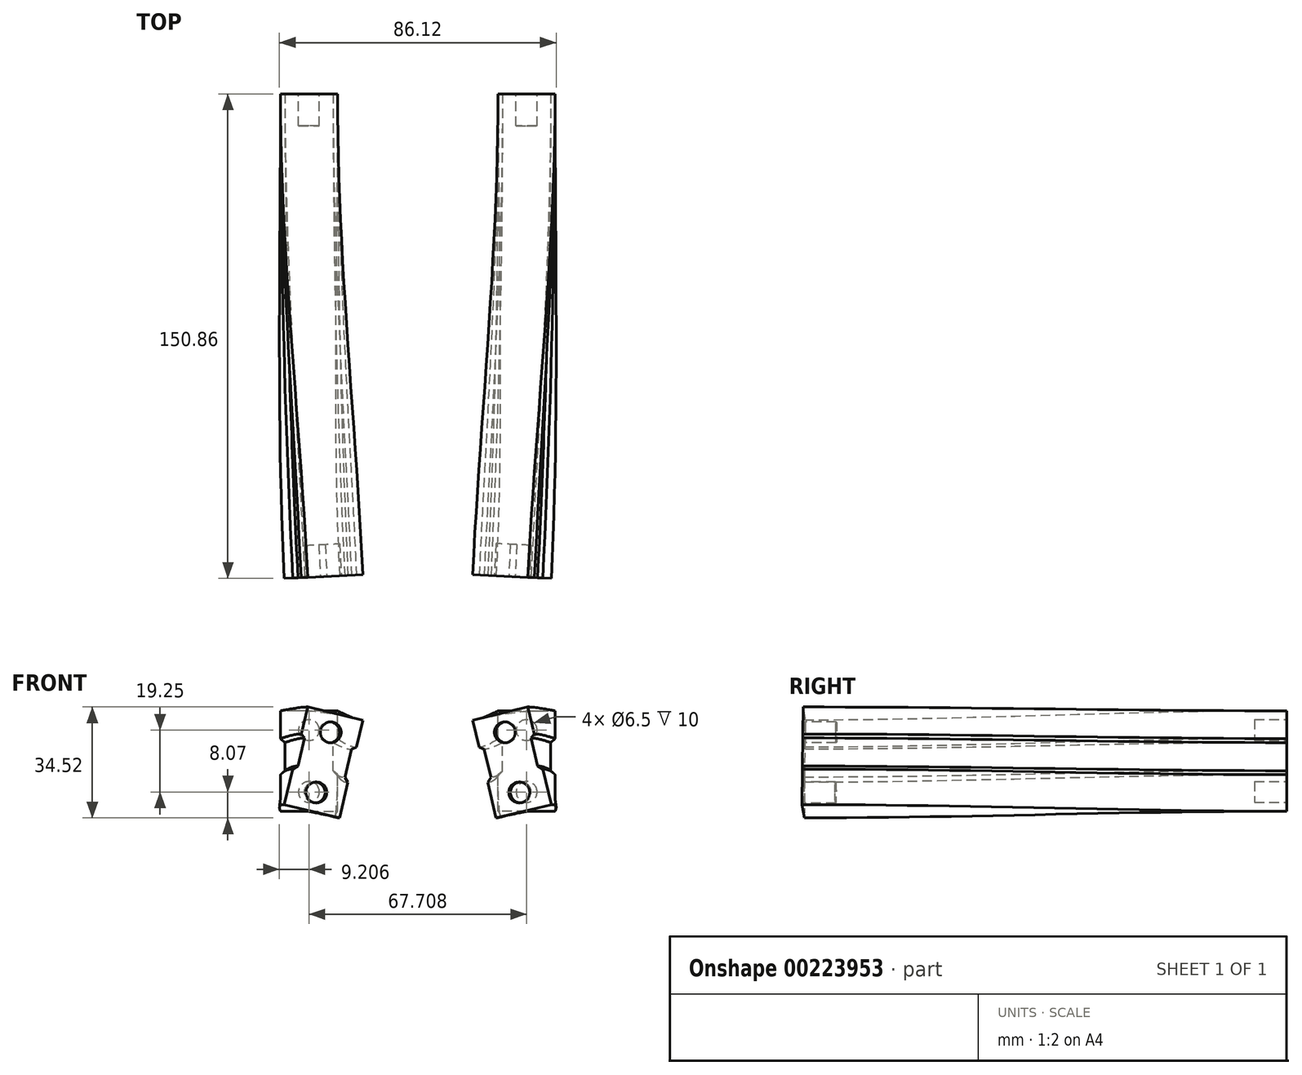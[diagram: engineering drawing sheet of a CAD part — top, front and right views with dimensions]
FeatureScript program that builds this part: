
annotation { "Feature Type Name" : "Feature", "Feature Type Description" : "" }
export const myFeature = defineFeature(function(context is Context, id is Id, definition is map)
    precondition{}
    {
        {
            var Q0;
            Q0=qCreatedBy(makeId("Front.planeOp"),FACE);
            var sketch = newSketch(context, id + "F0", { "sketchPlane" : qUnion([Q0])});
            skLineSegment(sketch, "E0.bottom", {"start": v(0, 0) * mm, "end": v(17.7, 0) * mm, "construction": true});
            skLineSegment(sketch, "E0.top", {"start": v(0, 31.25) * mm, "end": v(17.7, 31.25) * mm, "construction": true});
            skLineSegment(sketch, "E0.left", {"start": v(0, 0) * mm, "end": v(0, 31.25) * mm, "construction": true});
            skLineSegment(sketch, "E0.right", {"start": v(17.7, 0) * mm, "end": v(17.7, 31.25) * mm, "construction": true});
            skLineSegment(sketch, "E1", {"start": v(8.85, 31.25) * mm, "end": v(8.85, 0) * mm, "construction": true});
            skLineSegment(sketch, "E2", {"start": v(8.85, 0) * mm, "end": v(0, 0) * mm});
            skLineSegment(sketch, "E3", {"start": v(0, 11.35) * mm, "end": v(1.35, 12.6) * mm});
            skLineSegment(sketch, "E4", {"start": v(1.35, 12.6) * mm, "end": v(1.35, 21.35) * mm});
            skLineSegment(sketch, "E5", {"start": v(1.35, 21.35) * mm, "end": v(0, 22.6) * mm});
            skLineSegment(sketch, "E6", {"start": v(0, 22.6) * mm, "end": v(0, 31.25) * mm});
            skLineSegment(sketch, "E7", {"start": v(8.85, 31.25) * mm, "end": v(0, 31.25) * mm});
            skLineSegment(sketch, "E8", {"start": v(0, 0) * mm, "end": v(0, 11.35) * mm});
            skLineSegment(sketch, "E9.MirrorCS", {"start": v(16.35, 21.35) * mm, "end": v(17.7, 22.6) * mm});
            skLineSegment(sketch, "E10.MirrorCS", {"start": v(17.7, 11.35) * mm, "end": v(16.35, 12.6) * mm});
            skLineSegment(sketch, "E11.MirrorCS", {"start": v(17.7, 0) * mm, "end": v(17.7, 11.35) * mm});
            skLineSegment(sketch, "E12.MirrorCS", {"start": v(8.85, 31.25) * mm, "end": v(17.7, 31.25) * mm});
            skLineSegment(sketch, "E13.MirrorCS", {"start": v(8.85, 0) * mm, "end": v(17.7, 0) * mm});
            skLineSegment(sketch, "E14.MirrorCS", {"start": v(16.35, 12.6) * mm, "end": v(16.35, 21.35) * mm});
            skLineSegment(sketch, "E15.MirrorCS", {"start": v(17.7, 22.6) * mm, "end": v(17.7, 31.25) * mm});
            skLineSegment(sketch, "E16", {"start": v(0, 0) * mm, "end": v(17.22, -4.13) * mm, "construction": true});
            skSolve(sketch);
        }
        {
            var Q0;
            Q0=qCreatedBy(makeId("Top.planeOp"),FACE);
            var sketch = newSketch(context, id + "F1", { "sketchPlane" : qUnion([Q0])});
            skLineSegment(sketch, "E17", {"start": v(0, 0) * mm, "end": v(0, -150) * mm, "construction": true});
            skLineSegment(sketch, "E18", {"start": v(0, -150) * mm, "end": v(17.7, -150) * mm, "construction": true});
            skLineSegment(sketch, "E19", {"start": v(17.7, -150) * mm, "end": v(17.7, 0) * mm, "construction": true});
            skArc(sketch, "E20", {"start": v(0, -114.22) * mm, "mid": v(-0.22, -132.12) * mm, "end": v(-0.88, -150) * mm, "construction": true});
            skLineSegment(sketch, "E21", {"start": v(0, -114.22) * mm, "end": v(-729.17, -114.22) * mm, "construction": true});
            skLineSegment(sketch, "E22", {"start": v(-0.88, -150) * mm, "end": v(-729.17, -114.22) * mm, "construction": true});
            skLineSegment(sketch, "E23", {"start": v(0, -150) * mm, "end": v(-0.88, -150) * mm, "construction": true});
            skLineSegment(sketch, "E24", {"start": v(0, -114.22) * mm, "end": v(17.7, -114.22) * mm, "construction": true});
            skArc(sketch, "E25", {"start": v(17.7, -114.22) * mm, "mid": v(17.48, -132.55) * mm, "end": v(16.8, -150.87) * mm, "construction": true});
            skLineSegment(sketch, "E26", {"start": v(-0.88, -150) * mm, "end": v(16.8, -150.87) * mm, "construction": true});
            skPoint(sketch, "E27", {"position": v(7.97, -150.43) * mm});
            skSolve(sketch);
        }
        {
            var Q0;
            Q0=sQuery(id+"F1.wireOp",EDGE,"E26");
            var Q1;
            Q1=qCreatedBy(makeId("Front.planeOp"),FACE);
            cPlane(context, id + "F2", {"entities" : qUnion([Q0, Q1]), "cplaneType" : CPlaneType.LINE_ANGLE, "offset" : 25 * mm, "angle" : 0 * degree, "width" : 150 * mm, "height" : 150 * mm});
        }
        {
            var Q0;
            Q0=qCreatedBy(id+"F2.planeOp",FACE);
            var sketch = newSketch(context, id + "F3", { "sketchPlane" : qUnion([Q0])});
            skLineSegment(sketch, "E28.left", {"start": v(-23.95, 2.07) * mm, "end": v(-16.65, 32.45) * mm, "construction": true});
            skLineSegment(sketch, "E29", {"start": v(-8.04, 30.39) * mm, "end": v(-15.34, 0) * mm, "construction": true});
            skLineSegment(sketch, "E30", {"start": v(-15.34, 0) * mm, "end": v(-23.95, 2.07) * mm});
            skLineSegment(sketch, "E31", {"start": v(-21.3, 13.1) * mm, "end": v(-19.68, 14.05) * mm});
            skLineSegment(sketch, "E32", {"start": v(-19.68, 14.05) * mm, "end": v(-17.58, 22.8) * mm});
            skLineSegment(sketch, "E33", {"start": v(-17.58, 22.8) * mm, "end": v(-18.67, 24.05) * mm});
            skLineSegment(sketch, "E34", {"start": v(-18.67, 24.05) * mm, "end": v(-16.65, 32.45) * mm});
            skLineSegment(sketch, "E35", {"start": v(-8.04, 30.39) * mm, "end": v(-16.65, 32.45) * mm});
            skLineSegment(sketch, "E36", {"start": v(-23.95, 2.07) * mm, "end": v(-21.3, 13.1) * mm});
            skLineSegment(sketch, "E37.MirrorCS", {"start": v(-3, 19.3) * mm, "end": v(-1.45, 19.91) * mm});
            skLineSegment(sketch, "E38.MirrorCS", {"start": v(-4.08, 8.97) * mm, "end": v(-5.1, 10.54) * mm});
            skLineSegment(sketch, "E39.MirrorCS", {"start": v(-6.73, -2.07) * mm, "end": v(-4.08, 8.97) * mm});
            skLineSegment(sketch, "E40.MirrorCS", {"start": v(-8.04, 30.39) * mm, "end": v(0.57, 28.32) * mm});
            skLineSegment(sketch, "E41.MirrorCS", {"start": v(-15.34, 0) * mm, "end": v(-6.73, -2.07) * mm});
            skLineSegment(sketch, "E42.MirrorCS", {"start": v(-5.1, 10.54) * mm, "end": v(-3, 19.3) * mm});
            skLineSegment(sketch, "E43.MirrorCS", {"start": v(-1.45, 19.91) * mm, "end": v(0.57, 28.32) * mm});
            skLineSegment(sketch, "E44", {"start": v(-18.67, 24.05) * mm, "end": v(-17.35, 23.73) * mm, "construction": true});
            skLineSegment(sketch, "E45", {"start": v(-17.35, 23.73) * mm, "end": v(-17.58, 22.8) * mm, "construction": true});
            skLineSegment(sketch, "E46", {"start": v(-15.34, 0) * mm, "end": v(-24.2, 0) * mm, "construction": true});
            skSolve(sketch);
        }
        {
            var Q0;
            Q0 = qSketchRegion(id + "F0", true);
            var Q1;
            Q1 = qSketchRegion(id + "F3", true);
            loft(context, id + "F4", {"startCondition" : LoftEndDerivativeType.NORMAL_TO_PROFILE, "startMagnitude" : 1, "endCondition" : LoftEndDerivativeType.NORMAL_TO_PROFILE, "endMagnitude" : 1, "sheetProfilesArray" : [{ "sheetProfileEntities" : qUnion([Q0]) }, { "sheetProfileEntities" : qUnion([Q1]) }]});
        }
        {
            var Q0;
            Q0=makeQuery(id+"F4.opLoft","CAP_FACE",FACE,{"disambiguationData":[OSD([makeQuery(id+"F3.imprint","IMPRINT",FACE,{"disambiguationData":[TD([[makeQuery(id+"F3.imprint","IMPRINT",EDGE,{"derivedFrom":sQuery(id+"F3.wireOp",EDGE,"E30")}),-1.0]])]})])],"isStart":true});
            var sketch = newSketch(context, id + "F5", { "sketchPlane" : qUnion([Q0])});
            skLineSegment(sketch, "E47.bottom", {"start": v(-0.57, 28.32) * mm, "end": v(16.65, 32.45) * mm, "construction": true});
            skLineSegment(sketch, "E47.top", {"start": v(6.73, -2.07) * mm, "end": v(23.95, 2.07) * mm, "construction": true});
            skLineSegment(sketch, "E47.left", {"start": v(16.65, 32.45) * mm, "end": v(23.95, 2.07) * mm, "construction": true});
            skLineSegment(sketch, "E47.right", {"start": v(-0.57, 28.32) * mm, "end": v(6.73, -2.07) * mm, "construction": true});
            skLineSegment(sketch, "E48", {"start": v(8.04, 30.39) * mm, "end": v(15.34, 0) * mm, "construction": true});
            skCircle(sketch, "E49", {"center": v(13.94, 5.83) * mm, "radius": 3.25 * mm});
            skCircle(sketch, "E50", {"center": v(9.44, 24.55) * mm, "radius": 3.25 * mm});
            skSolve(sketch);
        }
        {
            var Q0;
            Q0 = qSketchRegion(id + "F5", true);
            extrude(context, id + "F6", {"entities" : qUnion([Q0]), "operationType" : NewBodyOperationType.REMOVE, "oppositeDirection" : true, "depth" : 10 * mm});
        }
        {
            var Q0;
            Q0=makeQuery(id+"F4.opLoft","CAP_FACE",FACE,{"disambiguationData":[OSD([makeQuery(id+"F0.imprint","IMPRINT",FACE,{"disambiguationData":[TD([[makeQuery(id+"F0.imprint","IMPRINT",EDGE,{"derivedFrom":sQuery(id+"F0.wireOp",EDGE,"E2")}),-1.0]])]})])],"isStart":true});
            var sketch = newSketch(context, id + "F7", { "sketchPlane" : qUnion([Q0])});
            skLineSegment(sketch, "E51.bottom", {"start": v(-17.7, 31.25) * mm, "end": v(0, 31.25) * mm, "construction": true});
            skLineSegment(sketch, "E51.top", {"start": v(-17.7, 0) * mm, "end": v(0, 0) * mm, "construction": true});
            skLineSegment(sketch, "E51.left", {"start": v(-17.7, 31.25) * mm, "end": v(-17.7, 0) * mm, "construction": true});
            skLineSegment(sketch, "E51.right", {"start": v(0, 31.25) * mm, "end": v(0, 0) * mm, "construction": true});
            skLineSegment(sketch, "E52", {"start": v(-8.85, 31.25) * mm, "end": v(-8.85, 0) * mm, "construction": true});
            skCircle(sketch, "E53", {"center": v(-8.85, 6) * mm, "radius": 3.25 * mm});
            skCircle(sketch, "E54", {"center": v(-8.85, 25.25) * mm, "radius": 3.25 * mm});
            skSolve(sketch);
        }
        {
            var Q0;
            Q0 = qSketchRegion(id + "F7", true);
            extrude(context, id + "F8", {"entities" : qUnion([Q0]), "operationType" : NewBodyOperationType.REMOVE, "oppositeDirection" : true, "depth" : 10 * mm});
        }
        {
            var Q0;
            Q0=makeQuery(id+"F4.opLoft","SWEPT_BODY",BODY,{"disambiguationData":[OSD([makeQuery(id+"F0.imprint","IMPRINT",FACE,{"disambiguationData":[TD([[makeQuery(id+"F0.imprint","IMPRINT",EDGE,{"derivedFrom":sQuery(id+"F0.wireOp",EDGE,"E2")}),-1.0]])]}),makeQuery(id+"F3.imprint","IMPRINT",FACE,{"disambiguationData":[TD([[makeQuery(id+"F3.imprint","IMPRINT",EDGE,{"derivedFrom":sQuery(id+"F3.wireOp",EDGE,"E30")}),-1.0]])]})])]});
            var Q1;
            Q1=qCreatedBy(makeId("Right.planeOp"),FACE);
            mirror(context, id + "F9", {"entities" : qUnion([Q0]), "mirrorPlane" : qUnion([Q1])});
        }
        {
            var Q0;
            Q0=makeQuery(id+"F9.opPattern","COPY",BODY,{"derivedFrom":makeQuery(id+"F4.opLoft","SWEPT_BODY",BODY,{"disambiguationData":[OSD([makeQuery(id+"F0.imprint","IMPRINT",FACE,{"disambiguationData":[TD([[makeQuery(id+"F0.imprint","IMPRINT",EDGE,{"derivedFrom":sQuery(id+"F0.wireOp",EDGE,"E2")}),-1.0]])]}),makeQuery(id+"F3.imprint","IMPRINT",FACE,{"disambiguationData":[TD([[makeQuery(id+"F3.imprint","IMPRINT",EDGE,{"derivedFrom":sQuery(id+"F3.wireOp",EDGE,"E30")}),-1.0]])]})])]}),"instanceName":"1"});
            transform(context, id + "F10", {"entities" : qUnion([Q0]), "transformType" : TransformType.TRANSLATION_3D, "dx" : -50 * mm, "dy" : 0 * mm, "dz" : 0 * mm, "makeCopy" : false});
        }
    });
